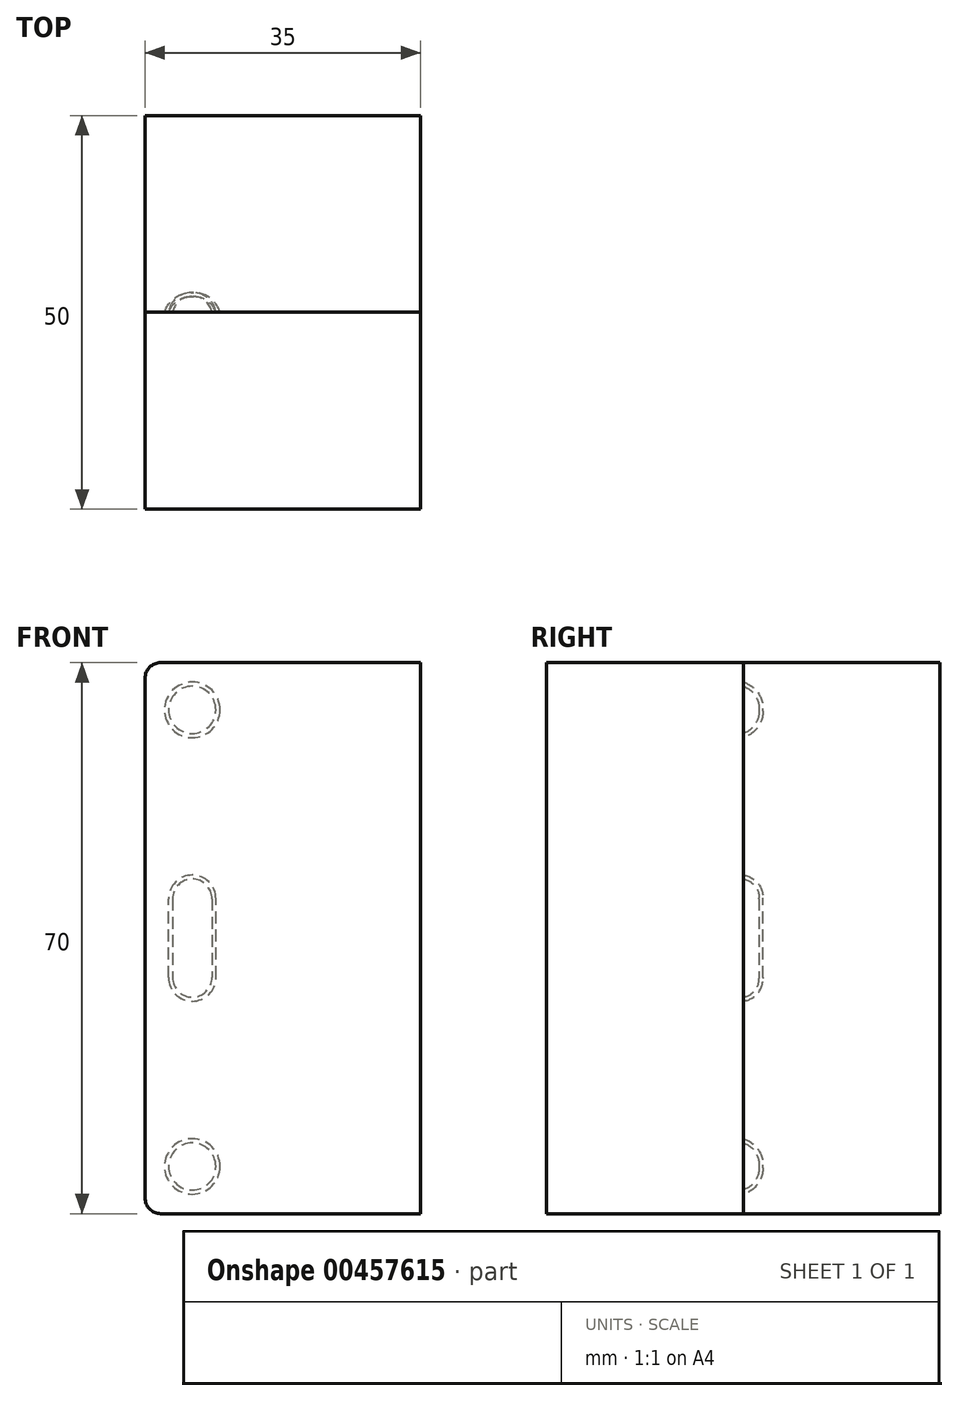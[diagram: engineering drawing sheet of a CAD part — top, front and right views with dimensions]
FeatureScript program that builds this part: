
annotation { "Feature Type Name" : "Feature", "Feature Type Description" : "" }
export const myFeature = defineFeature(function(context is Context, id is Id, definition is map)
    precondition{}
    {
        {
            var Q0;
            Q0=qCreatedBy(makeId("Front.planeOp"),FACE);
            var sketch = newSketch(context, id + "F0", { "sketchPlane" : qUnion([Q0])});
            skLineSegment(sketch, "E0.bottom", {"start": v(-35, 46) * mm, "end": v(35, 46) * mm});
            skLineSegment(sketch, "E0.top", {"start": v(-35, -24) * mm, "end": v(35, -24) * mm});
            skLineSegment(sketch, "E0.left", {"start": v(-35, 46) * mm, "end": v(-35, -24) * mm});
            skLineSegment(sketch, "E0.right", {"start": v(35, 46) * mm, "end": v(35, -24) * mm});
            skPoint(sketch, "E1", {"position": v(35, 11) * mm});
            skPoint(sketch, "E2", {"position": v(-35, 11) * mm});
            skLineSegment(sketch, "E3", {"start": v(-35, 11) * mm, "end": v(35, 11) * mm});
            skPoint(sketch, "E4", {"position": v(0, 11) * mm});
            skPoint(sketch, "E5", {"position": v(0, -24) * mm});
            skPoint(sketch, "E6", {"position": v(0, 46) * mm});
            skLineSegment(sketch, "E7", {"start": v(0, 46) * mm, "end": v(0, -24) * mm});
            skSolve(sketch);
        }
        {
            var Q0;
            {var subQ0=sQuery(id+"F0.wireOp",EDGE,"E0.bottom");Q0=makeQuery(id+"F0.imprint","IMPRINT",FACE,{"disambiguationData":[TD([[makeQuery(id+"F0.imprint","IMPRINT",EDGE,{"derivedFrom":subQ0}),-1.0]])]});}
            var Q1;
            {var subQ0=sQuery(id+"F0.wireOp",EDGE,"E0.top");Q1=makeQuery(id+"F0.imprint","IMPRINT",FACE,{"disambiguationData":[TD([[makeQuery(id+"F0.imprint","IMPRINT",EDGE,{"derivedFrom":subQ0}),1.0]])]});}
            extrude(context, id + "F1", {"entities" : qUnion([Q0, Q1]), "depth" : 25 * mm});
        }
        {
            var Q0;
            Q0=makeQuery(id+"F1.opExtrude","SWEPT_EDGE",EDGE,{"disambiguationData":[OSD([sQuery(id+"F0.wireOp",EDGE,"E0.bottom"),sQuery(id+"F0.wireOp",EDGE,"E0.right")])]});
            var Q1;
            Q1=makeQuery(id+"F1.opExtrude","SWEPT_EDGE",EDGE,{"disambiguationData":[OSD([sQuery(id+"F0.wireOp",EDGE,"E0.top"),sQuery(id+"F0.wireOp",EDGE,"E0.right")])]});
            var Q2;
            Q2=makeQuery(id+"F1.opExtrude","SWEPT_EDGE",EDGE,{"disambiguationData":[OSD([sQuery(id+"F0.wireOp",EDGE,"E0.bottom"),sQuery(id+"F0.wireOp",EDGE,"E0.left")])]});
            var Q3;
            Q3=makeQuery(id+"F1.opExtrude","SWEPT_EDGE",EDGE,{"disambiguationData":[OSD([sQuery(id+"F0.wireOp",EDGE,"E0.top"),sQuery(id+"F0.wireOp",EDGE,"E0.left")])]});
            fillet(context, id + "F2", {"entities" : qUnion([Q0, Q1, Q2, Q3]), "radius" : 2 * mm, "tangentPropagation" : true, "allowEdgeOverflow" : false});
        }
        {
            var Q0;
            Q0=makeQuery(id+"F1.opExtrude","CAP_FACE",FACE,{"disambiguationData":[OSD([sQuery(id+"F0.wireOp",EDGE,"E0.bottom"),sQuery(id+"F0.wireOp",EDGE,"E0.top"),sQuery(id+"F0.wireOp",EDGE,"E0.left"),sQuery(id+"F0.wireOp",EDGE,"E0.right")])],"isStart":true});
            var sketch = newSketch(context, id + "F3", { "sketchPlane" : qUnion([Q0])});
            skCircle(sketch, "E8", {"center": v(-29, -18) * mm, "radius": 3 * mm});
            skCircle(sketch, "E9", {"center": v(-29, 40) * mm, "radius": 3 * mm});
            skCircle(sketch, "E10", {"center": v(29, 40) * mm, "radius": 3 * mm});
            skCircle(sketch, "E11", {"center": v(29, -18) * mm, "radius": 3 * mm});
            skPoint(sketch, "E12", {"position": v(35, 11) * mm});
            skLineSegment(sketch, "E13", {"start": v(-29, 40) * mm, "end": v(-29, -18) * mm, "construction": true});
            skLineSegment(sketch, "E14", {"start": v(29, -18) * mm, "end": v(29, 40) * mm, "construction": true});
            skPoint(sketch, "E15", {"position": v(-35, 11) * mm});
            skPoint(sketch, "E16", {"position": v(-29, 11) * mm});
            skLineSegment(sketch, "E17.bottom", {"start": v(-31.5, 16) * mm, "end": v(-26.5, 16) * mm});
            skLineSegment(sketch, "E17.top", {"start": v(-31.5, 6) * mm, "end": v(-26.5, 6) * mm});
            skLineSegment(sketch, "E17.left", {"start": v(-31.5, 16) * mm, "end": v(-31.5, 6) * mm});
            skLineSegment(sketch, "E17.right", {"start": v(-26.5, 16) * mm, "end": v(-26.5, 6) * mm});
            skPoint(sketch, "E18", {"position": v(-29, 16) * mm});
            skPoint(sketch, "E19", {"position": v(-29, 6) * mm});
            skPoint(sketch, "E20", {"position": v(-31.5, 11) * mm});
            skPoint(sketch, "E21", {"position": v(-26.5, 11) * mm});
            skArc(sketch, "E22", {"start": v(-26.5, 16) * mm, "mid": v(-29, 18.5) * mm, "end": v(-31.5, 16) * mm});
            skArc(sketch, "E23", {"start": v(-31.5, 6) * mm, "mid": v(-29, 3.5) * mm, "end": v(-26.5, 6) * mm});
            skPoint(sketch, "E24", {"position": v(29, 11) * mm});
            skLineSegment(sketch, "E25.bottom", {"start": v(26.5, 16) * mm, "end": v(31.5, 16) * mm});
            skLineSegment(sketch, "E25.top", {"start": v(26.5, 6) * mm, "end": v(31.5, 6) * mm});
            skLineSegment(sketch, "E25.left", {"start": v(26.5, 16) * mm, "end": v(26.5, 6) * mm});
            skLineSegment(sketch, "E25.right", {"start": v(31.5, 16) * mm, "end": v(31.5, 6) * mm});
            skPoint(sketch, "E26", {"position": v(29, 16) * mm});
            skPoint(sketch, "E27", {"position": v(29, 6) * mm});
            skPoint(sketch, "E28", {"position": v(31.5, 11) * mm});
            skPoint(sketch, "E29", {"position": v(26.5, 11) * mm});
            skArc(sketch, "E30", {"start": v(31.5, 16) * mm, "mid": v(29, 18.5) * mm, "end": v(26.5, 16) * mm});
            skArc(sketch, "E31", {"start": v(26.5, 6) * mm, "mid": v(29, 3.5) * mm, "end": v(31.5, 6) * mm});
            skSolve(sketch);
        }
        {
            var Q0;
            Q0=makeQuery(id+"F3.imprint","IMPRINT",FACE,{"disambiguationData":[TD([[makeQuery(id+"F3.imprint","IMPRINT",EDGE,{"derivedFrom":sQuery(id+"F3.wireOp",EDGE,"E10")}),1.0]])]});
            var Q1;
            Q1=makeQuery(id+"F3.imprint","IMPRINT",FACE,{"disambiguationData":[TD([[makeQuery(id+"F3.imprint","IMPRINT",EDGE,{"derivedFrom":sQuery(id+"F3.wireOp",EDGE,"E9")}),1.0]])]});
            var Q2;
            Q2=makeQuery(id+"F3.imprint","IMPRINT",FACE,{"disambiguationData":[TD([[makeQuery(id+"F3.imprint","IMPRINT",EDGE,{"derivedFrom":sQuery(id+"F3.wireOp",EDGE,"E17.bottom")}),1.0]])]});
            var Q3;
            Q3=makeQuery(id+"F3.imprint","IMPRINT",FACE,{"disambiguationData":[TD([[makeQuery(id+"F3.imprint","IMPRINT",EDGE,{"derivedFrom":sQuery(id+"F3.wireOp",EDGE,"E17.bottom")}),-1.0]])]});
            var Q4;
            Q4=makeQuery(id+"F3.imprint","IMPRINT",FACE,{"disambiguationData":[TD([[makeQuery(id+"F3.imprint","IMPRINT",EDGE,{"derivedFrom":sQuery(id+"F3.wireOp",EDGE,"E17.top")}),-1.0]])]});
            var Q5;
            Q5=makeQuery(id+"F3.imprint","IMPRINT",FACE,{"disambiguationData":[TD([[makeQuery(id+"F3.imprint","IMPRINT",EDGE,{"derivedFrom":sQuery(id+"F3.wireOp",EDGE,"E25.top")}),-1.0]])]});
            var Q6;
            Q6=makeQuery(id+"F3.imprint","IMPRINT",FACE,{"disambiguationData":[TD([[makeQuery(id+"F3.imprint","IMPRINT",EDGE,{"derivedFrom":sQuery(id+"F3.wireOp",EDGE,"E25.bottom")}),-1.0]])]});
            var Q7;
            Q7=makeQuery(id+"F3.imprint","IMPRINT",FACE,{"disambiguationData":[TD([[makeQuery(id+"F3.imprint","IMPRINT",EDGE,{"derivedFrom":sQuery(id+"F3.wireOp",EDGE,"E25.bottom")}),1.0]])]});
            var Q8;
            Q8=makeQuery(id+"F3.imprint","IMPRINT",FACE,{"disambiguationData":[TD([[makeQuery(id+"F3.imprint","IMPRINT",EDGE,{"derivedFrom":sQuery(id+"F3.wireOp",EDGE,"E11")}),1.0]])]});
            var Q9;
            Q9=makeQuery(id+"F3.imprint","IMPRINT",FACE,{"disambiguationData":[TD([[makeQuery(id+"F3.imprint","IMPRINT",EDGE,{"derivedFrom":sQuery(id+"F3.wireOp",EDGE,"E8")}),1.0]])]});
            extrude(context, id + "F4", {"entities" : qUnion([Q0, Q1, Q2, Q3, Q4, Q5, Q6, Q7, Q8, Q9]), "operationType" : NewBodyOperationType.ADD, "depth" : 2 * mm});
        }
        {
            var Q0;
            Q0=makeQuery(id+"F4.opExtrude","CAP_EDGE",EDGE,{"disambiguationData":[OSD([sQuery(id+"F3.wireOp",EDGE,"E9")])],"isStart":false});
            var Q1;
            Q1=makeQuery(id+"F4.opExtrude","CAP_FACE",FACE,{"disambiguationData":[OSD([sQuery(id+"F3.wireOp",EDGE,"E8")])],"isStart":false});
            var Q2;
            Q2=makeQuery(id+"F4.opExtrude","CAP_FACE",FACE,{"disambiguationData":[OSD([sQuery(id+"F3.wireOp",EDGE,"E11")])],"isStart":false});
            var Q3;
            Q3=makeQuery(id+"F4.opExtrude","CAP_EDGE",EDGE,{"disambiguationData":[OSD([sQuery(id+"F3.wireOp",EDGE,"E10")])],"isStart":false});
            fillet(context, id + "F5", {"entities" : qUnion([Q0, Q1, Q2, Q3]), "radius" : 3 * mm, "tangentPropagation" : true, "allowEdgeOverflow" : false});
        }
        {
            var Q0;
            Q0=makeQuery(id+"F4.opExtrude","CAP_FACE",FACE,{"disambiguationData":[OSD([sQuery(id+"F3.wireOp",EDGE,"E17.left"),sQuery(id+"F3.wireOp",EDGE,"E17.right"),sQuery(id+"F3.wireOp",EDGE,"E22"),sQuery(id+"F3.wireOp",EDGE,"E23")])],"isStart":false});
            var Q1;
            Q1=makeQuery(id+"F4.opExtrude","CAP_FACE",FACE,{"disambiguationData":[OSD([sQuery(id+"F3.wireOp",EDGE,"E25.left"),sQuery(id+"F3.wireOp",EDGE,"E25.right"),sQuery(id+"F3.wireOp",EDGE,"E30"),sQuery(id+"F3.wireOp",EDGE,"E31")])],"isStart":false});
            fillet(context, id + "F6", {"entities" : qUnion([Q0, Q1]), "radius" : 2.4 * mm, "tangentPropagation" : true, "allowEdgeOverflow" : false});
        }
        {
            var Q0;
            {var subQ0=sQuery(id+"F0.wireOp",EDGE,"E0.bottom");Q0=makeQuery(id+"F0.imprint","IMPRINT",FACE,{"disambiguationData":[TD([[makeQuery(id+"F0.imprint","IMPRINT",EDGE,{"derivedFrom":subQ0}),-1.0]])]});}
            var Q1;
            {var subQ0=sQuery(id+"F0.wireOp",EDGE,"E0.top");Q1=makeQuery(id+"F0.imprint","IMPRINT",FACE,{"disambiguationData":[TD([[makeQuery(id+"F0.imprint","IMPRINT",EDGE,{"derivedFrom":subQ0}),1.0]])]});}
            extrude(context, id + "F7", {"entities" : qUnion([Q0, Q1]), "oppositeDirection" : true, "depth" : 25 * mm});
        }
        {
            var Q0;
            Q0=makeQuery(id+"F7.opExtrude","SWEPT_EDGE",EDGE,{"disambiguationData":[OSD([sQuery(id+"F0.wireOp",EDGE,"E0.bottom"),sQuery(id+"F0.wireOp",EDGE,"E0.left")])]});
            var Q1;
            Q1=makeQuery(id+"F7.opExtrude","SWEPT_EDGE",EDGE,{"disambiguationData":[OSD([sQuery(id+"F0.wireOp",EDGE,"E0.bottom"),sQuery(id+"F0.wireOp",EDGE,"E0.right")])]});
            var Q2;
            Q2=makeQuery(id+"F7.opExtrude","SWEPT_EDGE",EDGE,{"disambiguationData":[OSD([sQuery(id+"F0.wireOp",EDGE,"E0.top"),sQuery(id+"F0.wireOp",EDGE,"E0.right")])]});
            var Q3;
            Q3=makeQuery(id+"F7.opExtrude","SWEPT_EDGE",EDGE,{"disambiguationData":[OSD([sQuery(id+"F0.wireOp",EDGE,"E0.top"),sQuery(id+"F0.wireOp",EDGE,"E0.left")])]});
            fillet(context, id + "F8", {"entities" : qUnion([Q0, Q1, Q2, Q3]), "radius" : 2 * mm, "tangentPropagation" : true, "allowEdgeOverflow" : false});
        }
        {
            var Q0;
            Q0=makeQuery(id+"F1.opExtrude","SWEPT_BODY",BODY,{"disambiguationData":[OSD([sQuery(id+"F0.wireOp",EDGE,"E0.bottom"),sQuery(id+"F0.wireOp",EDGE,"E0.top"),sQuery(id+"F0.wireOp",EDGE,"E0.left"),sQuery(id+"F0.wireOp",EDGE,"E0.right")])]});
            var Q1;
            Q1=makeQuery(id+"F7.opExtrude","SWEPT_BODY",BODY,{"disambiguationData":[OSD([sQuery(id+"F0.wireOp",EDGE,"E0.bottom"),sQuery(id+"F0.wireOp",EDGE,"E0.top"),sQuery(id+"F0.wireOp",EDGE,"E0.left"),sQuery(id+"F0.wireOp",EDGE,"E0.right")])]});
            var Q2;
            Q2=makeQuery(id+"F5.opFillet","BLEND_FACE",FACE,{"disambiguationData":[OSD([sQuery(id+"F3.wireOp",EDGE,"E10")])]});
            var Q3;
            Q3=makeQuery(id+"F6.opFillet","BLEND_FACE",FACE,{"disambiguationData":[OSD([sQuery(id+"F3.wireOp",EDGE,"E25.right")])]});
            var Q4;
            Q4=makeQuery(id+"F6.opFillet","BLEND_FACE",FACE,{"disambiguationData":[OSD([sQuery(id+"F3.wireOp",EDGE,"E30")])]});
            var Q5;
            Q5=makeQuery(id+"F6.opFillet","BLEND_FACE",FACE,{"disambiguationData":[OSD([sQuery(id+"F3.wireOp",EDGE,"E25.left")])]});
            var Q6;
            Q6=makeQuery(id+"F6.opFillet","BLEND_FACE",FACE,{"disambiguationData":[OSD([sQuery(id+"F3.wireOp",EDGE,"E31")])]});
            var Q7;
            Q7=makeQuery(id+"F4.opExtrude","CAP_FACE",FACE,{"disambiguationData":[OSD([sQuery(id+"F3.wireOp",EDGE,"E25.left"),sQuery(id+"F3.wireOp",EDGE,"E25.right"),sQuery(id+"F3.wireOp",EDGE,"E30"),sQuery(id+"F3.wireOp",EDGE,"E31")])],"isStart":false});
            var Q8;
            Q8=makeQuery(id+"F5.opFillet","BLEND_FACE",FACE,{"disambiguationData":[OSD([sQuery(id+"F3.wireOp",EDGE,"E11")])]});
            var Q9;
            Q9=makeQuery(id+"F4.opExtrude","CAP_FACE",FACE,{"disambiguationData":[OSD([sQuery(id+"F3.wireOp",EDGE,"E17.left"),sQuery(id+"F3.wireOp",EDGE,"E17.right"),sQuery(id+"F3.wireOp",EDGE,"E22"),sQuery(id+"F3.wireOp",EDGE,"E23")])],"isStart":false});
            var Q10;
            Q10=makeQuery(id+"F6.opFillet","BLEND_FACE",FACE,{"disambiguationData":[OSD([sQuery(id+"F3.wireOp",EDGE,"E17.right")])]});
            var Q11;
            Q11=makeQuery(id+"F6.opFillet","BLEND_FACE",FACE,{"disambiguationData":[OSD([sQuery(id+"F3.wireOp",EDGE,"E17.left")])]});
            var Q12;
            Q12=makeQuery(id+"F6.opFillet","BLEND_FACE",FACE,{"disambiguationData":[OSD([sQuery(id+"F3.wireOp",EDGE,"E23")])]});
            var Q13;
            Q13=makeQuery(id+"F6.opFillet","BLEND_FACE",FACE,{"disambiguationData":[OSD([sQuery(id+"F3.wireOp",EDGE,"E22")])]});
            var Q14;
            Q14=makeQuery(id+"F5.opFillet","BLEND_FACE",FACE,{"disambiguationData":[OSD([sQuery(id+"F3.wireOp",EDGE,"E9")])]});
            var Q15;
            Q15=makeQuery(id+"F5.opFillet","BLEND_FACE",FACE,{"disambiguationData":[OSD([sQuery(id+"F3.wireOp",EDGE,"E8")])]});
            var Q16;
            Q16=makeQuery(id+"F4.opExtrude","CAP_FACE",FACE,{"disambiguationData":[OSD([sQuery(id+"F3.wireOp",EDGE,"E8")])],"isStart":false});
            var Q17;
            Q17=makeQuery(id+"F4.opExtrude","CAP_FACE",FACE,{"disambiguationData":[OSD([sQuery(id+"F3.wireOp",EDGE,"E9")])],"isStart":false});
            var Q18;
            Q18=makeQuery(id+"F4.opExtrude","CAP_FACE",FACE,{"disambiguationData":[OSD([sQuery(id+"F3.wireOp",EDGE,"E10")])],"isStart":false});
            var Q19;
            Q19=makeQuery(id+"F4.opExtrude","CAP_FACE",FACE,{"disambiguationData":[OSD([sQuery(id+"F3.wireOp",EDGE,"E11")])],"isStart":false});
            booleanBodies(context, id + "F9", {"operationType" : BooleanOperationType.SUBTRACTION, "tools" : qUnion([Q0]), "targets" : qUnion([Q1]), "offset" : true, "entitiesToOffset" : qUnion([Q2, Q3, Q4, Q5, Q6, Q7, Q8, Q9, Q10, Q11, Q12, Q13, Q14, Q15, Q16, Q17, Q18, Q19]), "offsetDistance" : 0.5 * mm, "keepTools" : true});
        }
        {
            var Q0;
            Q0=makeQuery(id+"F1.opExtrude","SWEPT_FACE",FACE,{"disambiguationData":[OSD([sQuery(id+"F0.wireOp",EDGE,"E0.right")])]});
            var sketch = newSketch(context, id + "F10", { "sketchPlane" : qUnion([Q0])});
            skPoint(sketch, "E32.0", {"position": v(-25, 46) * mm});
            skPoint(sketch, "E32.1", {"position": v(25, 46) * mm});
            skPoint(sketch, "E32.2", {"position": v(25, -24) * mm});
            skPoint(sketch, "E32.3", {"position": v(-25, -24) * mm});
            skLineSegment(sketch, "E33.bottom", {"start": v(-25, 46) * mm, "end": v(25, 46) * mm});
            skLineSegment(sketch, "E33.top", {"start": v(-25, -24) * mm, "end": v(25, -24) * mm});
            skLineSegment(sketch, "E33.left", {"start": v(-25, 46) * mm, "end": v(-25, -24) * mm});
            skLineSegment(sketch, "E33.right", {"start": v(25, 46) * mm, "end": v(25, -24) * mm});
            skSolve(sketch);
        }
        {
            var Q0;
            Q0 = qSketchRegion(id + "F10", true);
            extrude(context, id + "F11", {"entities" : qUnion([Q0]), "operationType" : NewBodyOperationType.REMOVE, "oppositeDirection" : true, "depth" : 35 * mm, "offsetDistance" : 25 * mm});
        }
    });
